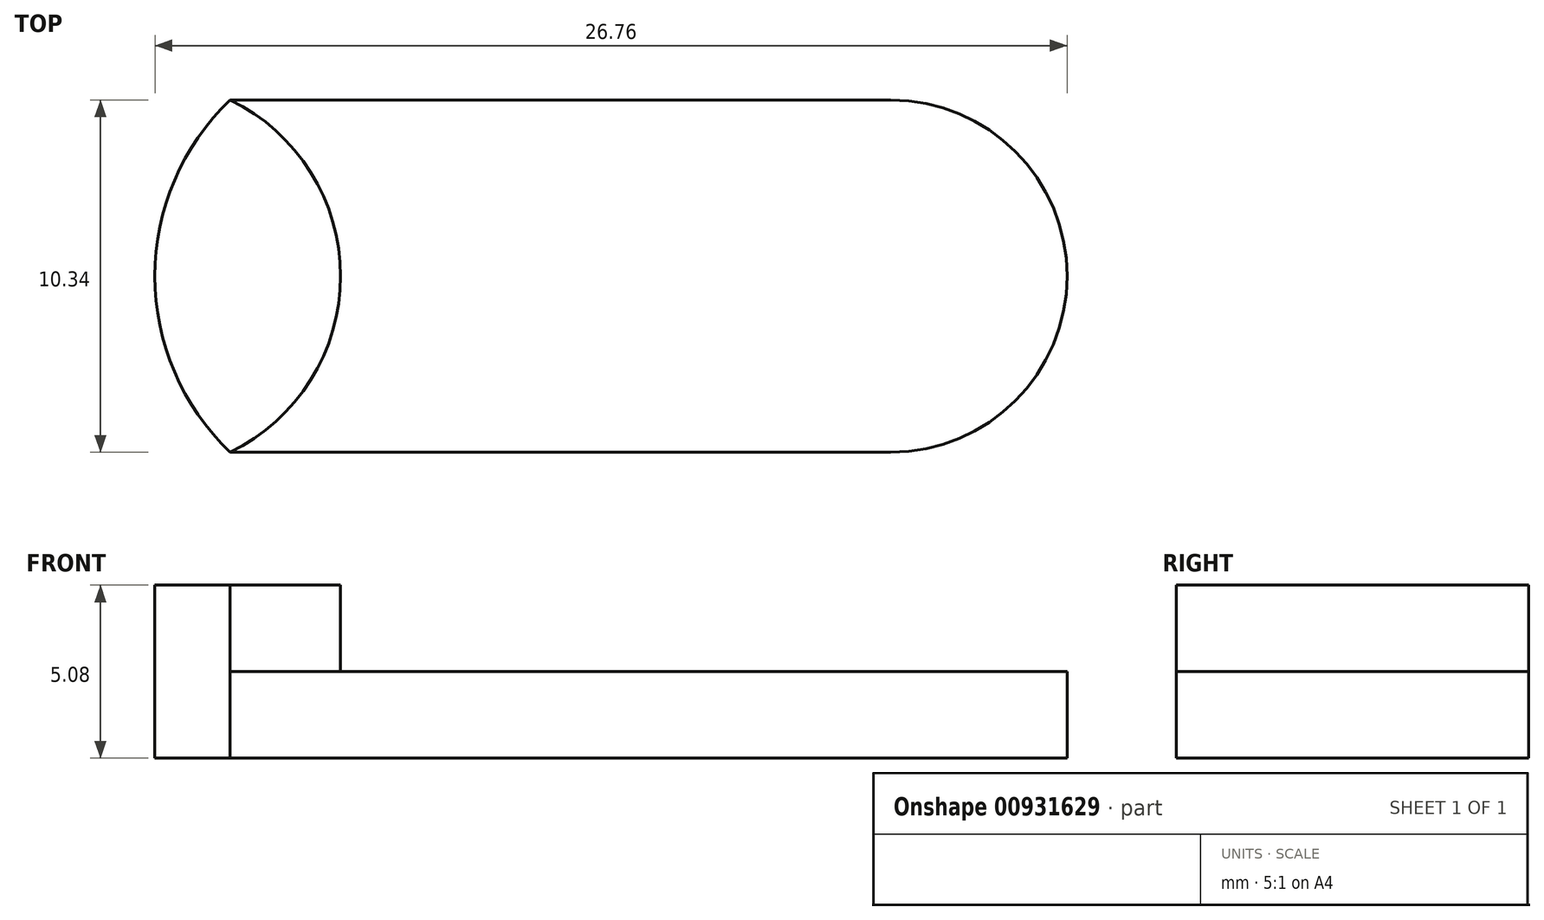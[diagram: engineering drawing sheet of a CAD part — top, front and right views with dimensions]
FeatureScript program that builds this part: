
annotation { "Feature Type Name" : "Feature", "Feature Type Description" : "" }
export const myFeature = defineFeature(function(context is Context, id is Id, definition is map)
    precondition{}
    {
        {
            var Q0;
            Q0=qCreatedBy(makeId("Top.planeOp"),FACE);
            var sketch = newSketch(context, id + "F0", { "sketchPlane" : qUnion([Q0])});
            skLineSegment(sketch, "E0.bottom", {"start": v(-27.65, 16.48) * mm, "end": v(-8.26, 16.48) * mm});
            skLineSegment(sketch, "E0.top", {"start": v(-27.65, 6.14) * mm, "end": v(-8.26, 6.14) * mm});
            skLineSegment(sketch, "E0.left", {"start": v(-27.65, 16.48) * mm, "end": v(-27.65, 6.14) * mm});
            skLineSegment(sketch, "E0.right", {"start": v(-8.26, 16.48) * mm, "end": v(-8.26, 6.14) * mm});
            skArc(sketch, "E1", {"start": v(-8.26, 6.14) * mm, "mid": v(-3.1, 11.31) * mm, "end": v(-8.26, 16.48) * mm});
            skArc(sketch, "E2", {"start": v(-27.65, 16.48) * mm, "mid": v(-29.85, 11.31) * mm, "end": v(-27.65, 6.14) * mm});
            skArc(sketch, "E3", {"start": v(-27.65, 6.14) * mm, "mid": v(-22.47, 11.31) * mm, "end": v(-27.65, 16.48) * mm});
            skSolve(sketch);
        }
        {
            var Q0;
            Q0=makeQuery(id+"F0.imprint","IMPRINT",FACE,{"disambiguationData":[TD([[makeQuery(id+"F0.imprint","IMPRINT",EDGE,{"derivedFrom":sQuery(id+"F0.wireOp",EDGE,"E0.left")}),-1.0]])]});
            var Q1;
            Q1=makeQuery(id+"F0.imprint","IMPRINT",FACE,{"disambiguationData":[TD([[makeQuery(id+"F0.imprint","IMPRINT",EDGE,{"derivedFrom":sQuery(id+"F0.wireOp",EDGE,"E0.right")}),1.0]])]});
            var Q2;
            Q2=makeQuery(id+"F0.imprint","IMPRINT",FACE,{"disambiguationData":[TD([[makeQuery(id+"F0.imprint","IMPRINT",EDGE,{"derivedFrom":sQuery(id+"F0.wireOp",EDGE,"E0.left")}),1.0]])]});
            var Q3;
            Q3=makeQuery(id+"F0.imprint","IMPRINT",FACE,{"disambiguationData":[TD([[makeQuery(id+"F0.imprint","IMPRINT",EDGE,{"derivedFrom":sQuery(id+"F0.wireOp",EDGE,"E0.bottom")}),-1.0]])]});
            extrude(context, id + "F1", {"entities" : qUnion([Q0, Q1, Q2, Q3]), "endBound" : BoundingType.SYMMETRIC, "depth" : 2.54 * mm, "offsetDistance" : 25.4 * mm});
        }
        {
            var Q0;
            Q0=makeQuery(id+"F1.opExtrude","CAP_FACE",FACE,{"disambiguationData":[OSD([sQuery(id+"F0.wireOp",EDGE,"E0.bottom"),sQuery(id+"F0.wireOp",EDGE,"E0.top"),sQuery(id+"F0.wireOp",EDGE,"E1"),sQuery(id+"F0.wireOp",EDGE,"E2")])],"isStart":false});
            var sketch = newSketch(context, id + "F2", { "sketchPlane" : qUnion([Q0])});
            skArc(sketch, "E4", {"start": v(-27.65, 6.14) * mm, "mid": v(-24.4, 11.31) * mm, "end": v(-27.65, 16.48) * mm});
            skSolve(sketch);
        }
        {
            var Q0;
            Q0=makeQuery(id+"F2.imprint","IMPRINT",FACE,{"disambiguationData":[TD([[makeQuery(id+"F2.imprint","IMPRINT",EDGE,{"derivedFrom":sQuery(id+"F2.wireOp",EDGE,"E4")}),1.0]])]});
            extrude(context, id + "F3", {"entities" : qUnion([Q0]), "operationType" : NewBodyOperationType.ADD, "endBound" : BoundingType.SYMMETRIC, "depth" : 5.08 * mm, "offsetDistance" : 25.4 * mm});
        }
    });
